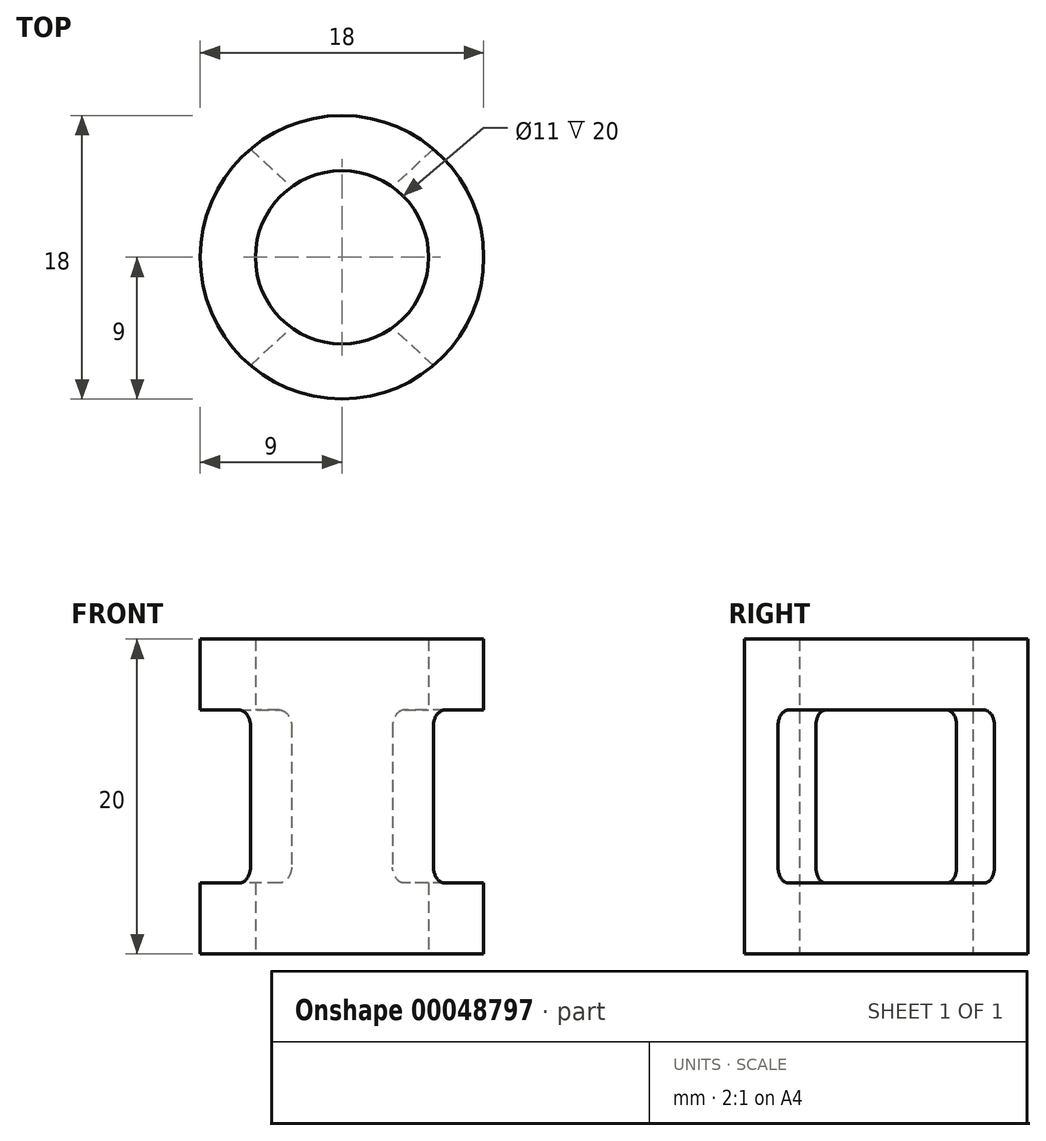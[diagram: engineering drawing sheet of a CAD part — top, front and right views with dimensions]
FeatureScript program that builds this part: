
annotation { "Feature Type Name" : "Feature", "Feature Type Description" : "" }
export const myFeature = defineFeature(function(context is Context, id is Id, definition is map)
    precondition{}
    {
        {
            var Q0;
            Q0=qCreatedBy(makeId("Top.planeOp"),FACE);
            var sketch = newSketch(context, id + "F0", { "sketchPlane" : qUnion([Q0])});
            skCircle(sketch, "E0", {"center": v(0, 0) * mm, "radius": 5.5 * mm});
            skCircle(sketch, "E1", {"center": v(0, 0) * mm, "radius": 9 * mm});
            skSolve(sketch);
        }
        {
            var Q0;
            Q0=makeQuery(id+"F0.imprint","IMPRINT",FACE,{"disambiguationData":[TD([[makeQuery(id+"F0.imprint","IMPRINT",EDGE,{"derivedFrom":sQuery(id+"F0.wireOp",EDGE,"E0")}),-1.0]])]});
            extrude(context, id + "F1", {"entities" : qUnion([Q0]), "depth" : 20 * mm});
        }
        {
            var Q0;
            Q0=qCreatedBy(makeId("Right.planeOp"),FACE);
            var sketch = newSketch(context, id + "F2", { "sketchPlane" : qUnion([Q0])});
            skPoint(sketch, "E2", {"position": v(0, 10) * mm});
            skLineSegment(sketch, "E3.bottom", {"start": v(1.5, 4.5) * mm, "end": v(-1.5, 4.5) * mm});
            skLineSegment(sketch, "E3.top", {"start": v(1.5, 15.5) * mm, "end": v(-1.5, 15.5) * mm});
            skLineSegment(sketch, "E3.left", {"start": v(1.5, 4.5) * mm, "end": v(1.5, 15.5) * mm});
            skLineSegment(sketch, "E3.right", {"start": v(-1.5, 4.5) * mm, "end": v(-1.5, 15.5) * mm});
            skSolve(sketch);
        }
        {
            var Q0;
            Q0=qCreatedBy(makeId("Right.planeOp"),FACE);
            cPlane(context, id + "F3", {"entities" : qUnion([Q0]), "cplaneType" : CPlaneType.OFFSET, "offset" : 20 * mm, "width" : 150 * mm, "height" : 150 * mm});
        }
        {
            var Q0;
            Q0=qCreatedBy(id+"F3.planeOp",FACE);
            var sketch = newSketch(context, id + "F4", { "sketchPlane" : qUnion([Q0])});
            skPoint(sketch, "E4", {"position": v(0, 10) * mm});
            skLineSegment(sketch, "E5.bottom", {"start": v(20, 4.5) * mm, "end": v(-20, 4.5) * mm});
            skLineSegment(sketch, "E5.top", {"start": v(20, 15.5) * mm, "end": v(-20, 15.5) * mm});
            skLineSegment(sketch, "E5.left", {"start": v(20, 4.5) * mm, "end": v(20, 15.5) * mm});
            skLineSegment(sketch, "E5.right", {"start": v(-20, 4.5) * mm, "end": v(-20, 15.5) * mm});
            skSolve(sketch);
        }
        {
            var Q0;
            Q0=qCreatedBy(id+"F3.planeOp",FACE);
            cPlane(context, id + "F5", {"entities" : qUnion([Q0]), "cplaneType" : CPlaneType.OFFSET, "offset" : 40 * mm, "oppositeDirection" : true, "width" : 150 * mm, "height" : 150 * mm});
        }
        {
            var Q0;
            Q0=qCreatedBy(id+"F5.planeOp",FACE);
            var sketch = newSketch(context, id + "F6", { "sketchPlane" : qUnion([Q0])});
            skPoint(sketch, "E6", {"position": v(0, 10) * mm});
            skLineSegment(sketch, "E7.bottom", {"start": v(20, 4.5) * mm, "end": v(-20, 4.5) * mm});
            skLineSegment(sketch, "E7.top", {"start": v(20, 15.5) * mm, "end": v(-20, 15.5) * mm});
            skLineSegment(sketch, "E7.left", {"start": v(20, 4.5) * mm, "end": v(20, 15.5) * mm});
            skLineSegment(sketch, "E7.right", {"start": v(-20, 4.5) * mm, "end": v(-20, 15.5) * mm});
            skSolve(sketch);
        }
        {
            var Q1;
            Q1=makeQuery(id+"F2.imprint","IMPRINT",FACE,{"disambiguationData":[TD([[makeQuery(id+"F2.imprint","IMPRINT",EDGE,{"derivedFrom":sQuery(id+"F2.wireOp",EDGE,"E3.bottom")}),-1.0]])]});
            var Q2;
            Q2=makeQuery(id+"F4.imprint","IMPRINT",FACE,{"disambiguationData":[TD([[makeQuery(id+"F4.imprint","IMPRINT",EDGE,{"derivedFrom":sQuery(id+"F4.wireOp",EDGE,"E5.bottom")}),-1.0]])]});
            loft(context, id + "F7", {"operationType" : NewBodyOperationType.REMOVE, "sheetProfilesArray" : [{ "sheetProfileEntities" : qUnion([Q1]) }, { "sheetProfileEntities" : qUnion([Q2]) }]});
        }
        {
            var Q1;
            Q1 = qSketchRegion(id + "F2", true);
            var Q2;
            Q2 = qSketchRegion(id + "F6", true);
            loft(context, id + "F8", {"operationType" : NewBodyOperationType.REMOVE, "sheetProfilesArray" : [{ "sheetProfileEntities" : qUnion([Q1]) }, { "sheetProfileEntities" : qUnion([Q2]) }]});
        }
        {
            var Q0;
            Q0=makeQuery(id+"F7.boolean.opBoolean","COPY",EDGE,{"derivedFrom":makeQuery(id+"F7.opLoft","SWEPT_EDGE",EDGE,{"disambiguationData":[OSD([sQuery(id+"F2.wireOp",EDGE,"E3.top"),sQuery(id+"F2.wireOp",EDGE,"E3.right"),sQuery(id+"F4.wireOp",EDGE,"E5.top"),sQuery(id+"F4.wireOp",EDGE,"E5.right")])]})});
            var Q1;
            Q1=makeQuery(id+"F7.boolean.opBoolean","COPY",EDGE,{"derivedFrom":makeQuery(id+"F7.opLoft","SWEPT_EDGE",EDGE,{"disambiguationData":[OSD([sQuery(id+"F2.wireOp",EDGE,"E3.top"),sQuery(id+"F2.wireOp",EDGE,"E3.left"),sQuery(id+"F4.wireOp",EDGE,"E5.top"),sQuery(id+"F4.wireOp",EDGE,"E5.left")])]})});
            var Q2;
            Q2=makeQuery(id+"F7.boolean.opBoolean","COPY",EDGE,{"derivedFrom":makeQuery(id+"F7.opLoft","SWEPT_EDGE",EDGE,{"disambiguationData":[OSD([sQuery(id+"F2.wireOp",EDGE,"E3.bottom"),sQuery(id+"F2.wireOp",EDGE,"E3.left"),sQuery(id+"F4.wireOp",EDGE,"E5.bottom"),sQuery(id+"F4.wireOp",EDGE,"E5.left")])]})});
            var Q3;
            Q3=makeQuery(id+"F7.boolean.opBoolean","COPY",EDGE,{"derivedFrom":makeQuery(id+"F7.opLoft","SWEPT_EDGE",EDGE,{"disambiguationData":[OSD([sQuery(id+"F2.wireOp",EDGE,"E3.bottom"),sQuery(id+"F2.wireOp",EDGE,"E3.right"),sQuery(id+"F4.wireOp",EDGE,"E5.bottom"),sQuery(id+"F4.wireOp",EDGE,"E5.right")])]})});
            var Q4;
            Q4=makeQuery(id+"F8.boolean.opBoolean","COPY",EDGE,{"derivedFrom":makeQuery(id+"F8.opLoft","SWEPT_EDGE",EDGE,{"disambiguationData":[OSD([sQuery(id+"F2.wireOp",EDGE,"E3.bottom"),sQuery(id+"F2.wireOp",EDGE,"E3.left"),sQuery(id+"F6.wireOp",EDGE,"E7.bottom"),sQuery(id+"F6.wireOp",EDGE,"E7.left")])]})});
            var Q5;
            Q5=makeQuery(id+"F8.boolean.opBoolean","COPY",EDGE,{"derivedFrom":makeQuery(id+"F8.opLoft","SWEPT_EDGE",EDGE,{"disambiguationData":[OSD([sQuery(id+"F2.wireOp",EDGE,"E3.bottom"),sQuery(id+"F2.wireOp",EDGE,"E3.right"),sQuery(id+"F6.wireOp",EDGE,"E7.bottom"),sQuery(id+"F6.wireOp",EDGE,"E7.right")])]})});
            var Q6;
            Q6=makeQuery(id+"F8.boolean.opBoolean","COPY",EDGE,{"derivedFrom":makeQuery(id+"F8.opLoft","SWEPT_EDGE",EDGE,{"disambiguationData":[OSD([sQuery(id+"F2.wireOp",EDGE,"E3.top"),sQuery(id+"F2.wireOp",EDGE,"E3.right"),sQuery(id+"F6.wireOp",EDGE,"E7.top"),sQuery(id+"F6.wireOp",EDGE,"E7.right")])]})});
            var Q7;
            Q7=makeQuery(id+"F8.boolean.opBoolean","COPY",EDGE,{"derivedFrom":makeQuery(id+"F8.opLoft","SWEPT_EDGE",EDGE,{"disambiguationData":[OSD([sQuery(id+"F2.wireOp",EDGE,"E3.top"),sQuery(id+"F2.wireOp",EDGE,"E3.left"),sQuery(id+"F6.wireOp",EDGE,"E7.top"),sQuery(id+"F6.wireOp",EDGE,"E7.left")])]})});
            fillet(context, id + "F9", {"entities" : qUnion([Q0, Q1, Q2, Q3, Q4, Q5, Q6, Q7]), "radius" : 1 * mm, "tangentPropagation" : true, "allowEdgeOverflow" : false});
        }
    });
